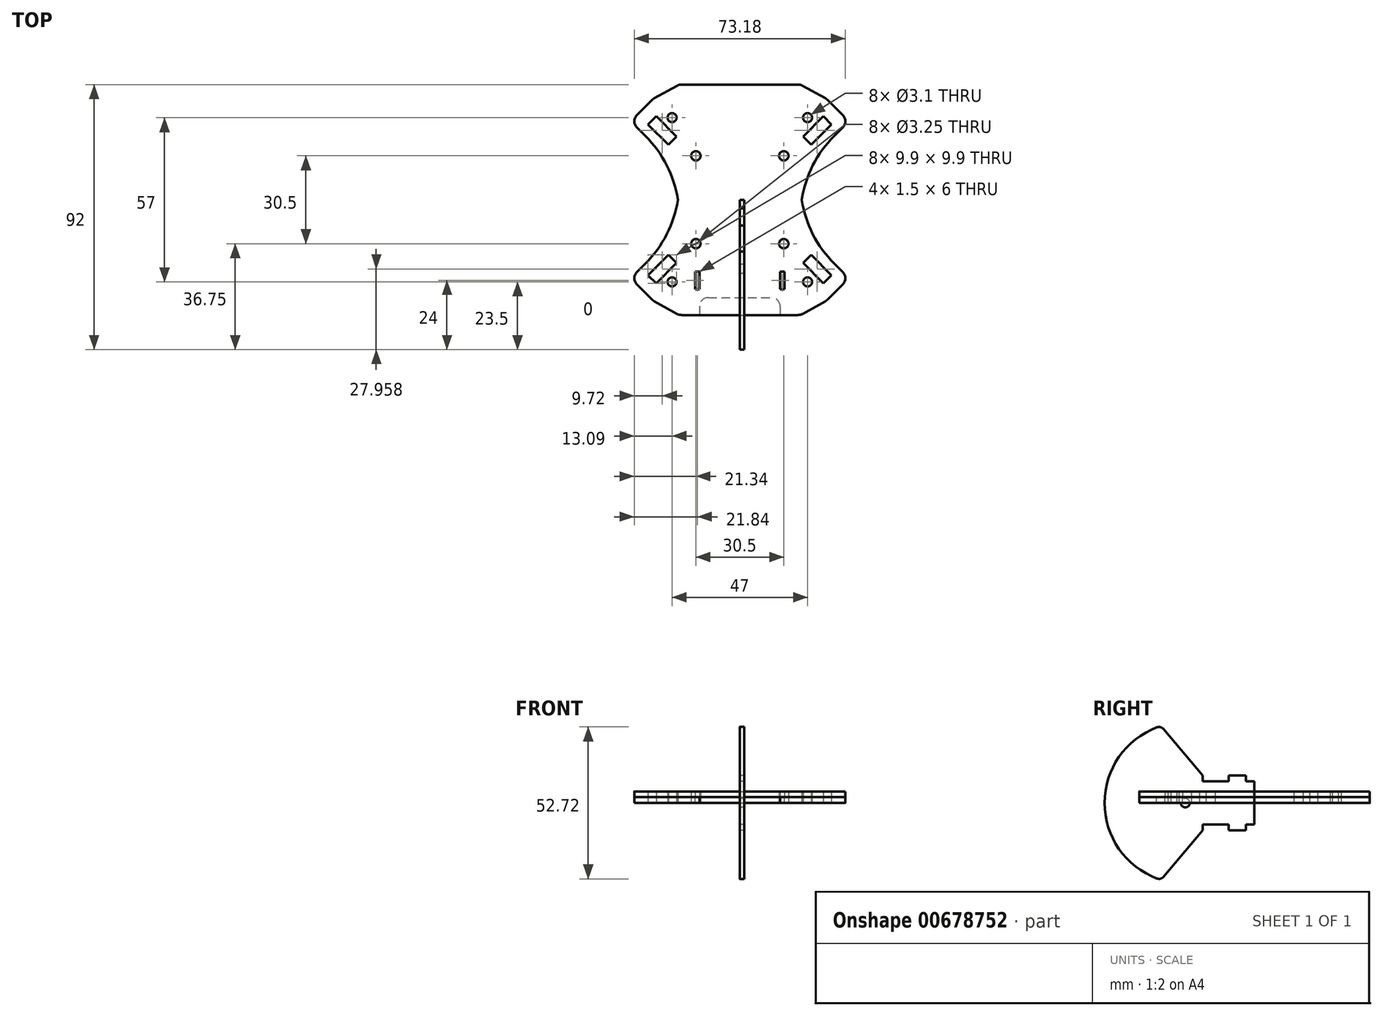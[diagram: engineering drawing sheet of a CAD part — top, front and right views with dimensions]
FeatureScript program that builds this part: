
annotation { "Feature Type Name" : "Feature", "Feature Type Description" : "" }
export const myFeature = defineFeature(function(context is Context, id is Id, definition is map)
    precondition{}
    {
        {
            var Q0;
            Q0=qCreatedBy(makeId("Top.planeOp"),FACE);
            var sketch = newSketch(context, id + "F0", { "sketchPlane" : qUnion([Q0])});
            skLineSegment(sketch, "E0.bottom", {"start": v(-18, 18) * mm, "end": v(18, 18) * mm, "construction": true});
            skLineSegment(sketch, "E0.top", {"start": v(-18, -18) * mm, "end": v(18, -18) * mm, "construction": true});
            skLineSegment(sketch, "E0.left", {"start": v(-18, 18) * mm, "end": v(-18, -18) * mm, "construction": true});
            skLineSegment(sketch, "E0.right", {"start": v(18, 18) * mm, "end": v(18, -18) * mm, "construction": true});
            skPoint(sketch, "E0.middle", {"position": v(0, 0) * mm});
            skLineSegment(sketch, "E1.bottom", {"start": v(-21, 40) * mm, "end": v(0, 40) * mm});
            skCircle(sketch, "E2", {"center": v(-74.25, 74.25) * mm, "radius": 64.25 * mm, "construction": true});
            skCircle(sketch, "E3", {"center": v(-15.25, 15.25) * mm, "radius": 1.63 * mm});
            skLineSegment(sketch, "E4", {"start": v(-15.25, 15.25) * mm, "end": v(0, 0) * mm, "construction": true});
            skLineSegment(sketch, "E5", {"start": v(-74.25, 74.25) * mm, "end": v(0, 0) * mm, "construction": true});
            skLineSegment(sketch, "E6", {"start": v(-32.53, 32.53) * mm, "end": v(-37.83, 27.22) * mm});
            skLineSegment(sketch, "E7", {"start": v(-37.83, 27.22) * mm, "end": v(-32.72, 22.1) * mm});
            skLineSegment(sketch, "E8.trimOffspring", {"start": v(-21, 0) * mm, "end": v(-21, -6.18) * mm});
            skPoint(sketch, "E9.visualSharp", {"position": v(-21, 10.4) * mm});
            skArc(sketch, "E9.filletArc", {"start": v(-21, -6.18) * mm, "mid": v(-24.04, 9.13) * mm, "end": v(-32.72, 22.1) * mm});
            skLineSegment(sketch, "E10", {"start": v(-29, 29) * mm, "end": v(-31.82, 26.16) * mm});
            skLineSegment(sketch, "E11", {"start": v(-31.82, 26.16) * mm, "end": v(-24.75, 19.1) * mm});
            skLineSegment(sketch, "E12", {"start": v(-24.75, 19.1) * mm, "end": v(-21.92, 21.92) * mm});
            skLineSegment(sketch, "E13", {"start": v(-21.92, 21.92) * mm, "end": v(-29, 29) * mm});
            skCircle(sketch, "E14", {"center": v(-23.5, 28.5) * mm, "radius": 1.55 * mm});
            skLineSegment(sketch, "E15", {"start": v(0, 40) * mm, "end": v(0, 0) * mm});
            skLineSegment(sketch, "E16", {"start": v(0, 0) * mm, "end": v(-21, 0) * mm});
            skLineSegment(sketch, "E17", {"start": v(-32.53, 32.53) * mm, "end": v(-30.05, 35) * mm});
            skLineSegment(sketch, "E18", {"start": v(-30.05, 35) * mm, "end": v(-21, 40) * mm});
            skSolve(sketch);
        }
        {
            var Q0;
            Q0=makeQuery(id+"F0.imprint","IMPRINT",FACE,{"disambiguationData":[TD([[makeQuery(id+"F0.imprint","IMPRINT",EDGE,{"derivedFrom":sQuery(id+"F0.wireOp",EDGE,"E1.bottom")}),-1.0]])]});
            extrude(context, id + "F1", {"entities" : qUnion([Q0]), "depth" : 2 * mm, "offsetDistance" : 25 * mm});
        }
        {
            var Q0;
            Q0=makeQuery(id+"F1.opExtrude","SWEPT_BODY",BODY,{"disambiguationData":[OSD([sQuery(id+"F0.wireOp",EDGE,"E1.bottom"),sQuery(id+"F0.wireOp",EDGE,"E3"),sQuery(id+"F0.wireOp",EDGE,"E6"),sQuery(id+"F0.wireOp",EDGE,"E7"),sQuery(id+"F0.wireOp",EDGE,"E8.trimOffspring"),sQuery(id+"F0.wireOp",EDGE,"E9.filletArc"),sQuery(id+"F0.wireOp",EDGE,"E10"),sQuery(id+"F0.wireOp",EDGE,"E11"),sQuery(id+"F0.wireOp",EDGE,"E12"),sQuery(id+"F0.wireOp",EDGE,"E13"),sQuery(id+"F0.wireOp",EDGE,"E14"),sQuery(id+"F0.wireOp",EDGE,"E15"),sQuery(id+"F0.wireOp",EDGE,"E16"),sQuery(id+"F0.wireOp",EDGE,"E17"),sQuery(id+"F0.wireOp",EDGE,"E18")])]});
            var Q1;
            Q1=qCreatedBy(makeId("Right.planeOp"),FACE);
            mirror(context, id + "F2", {"operationType" : NewBodyOperationType.ADD, "entities" : qUnion([Q0]), "mirrorPlane" : qUnion([Q1])});
        }
        {
            var Q0;
            Q0=makeQuery(id+"F1.opExtrude","SWEPT_BODY",BODY,{"disambiguationData":[OSD([sQuery(id+"F0.wireOp",EDGE,"E1.bottom"),sQuery(id+"F0.wireOp",EDGE,"E3"),sQuery(id+"F0.wireOp",EDGE,"E6"),sQuery(id+"F0.wireOp",EDGE,"E7"),sQuery(id+"F0.wireOp",EDGE,"E8.trimOffspring"),sQuery(id+"F0.wireOp",EDGE,"E9.filletArc"),sQuery(id+"F0.wireOp",EDGE,"E10"),sQuery(id+"F0.wireOp",EDGE,"E11"),sQuery(id+"F0.wireOp",EDGE,"E12"),sQuery(id+"F0.wireOp",EDGE,"E13"),sQuery(id+"F0.wireOp",EDGE,"E14"),sQuery(id+"F0.wireOp",EDGE,"E15"),sQuery(id+"F0.wireOp",EDGE,"E16"),sQuery(id+"F0.wireOp",EDGE,"E17"),sQuery(id+"F0.wireOp",EDGE,"E18")])]});
            var Q1;
            Q1=qCreatedBy(makeId("Front.planeOp"),FACE);
            mirror(context, id + "F3", {"operationType" : NewBodyOperationType.ADD, "entities" : qUnion([Q0]), "mirrorPlane" : qUnion([Q1])});
        }
        {
            var Q0;
            Q0=makeQuery(id+"F1.opExtrude","SWEPT_EDGE",EDGE,{"disambiguationData":[OSD([sQuery(id+"F0.wireOp",EDGE,"E6"),sQuery(id+"F0.wireOp",EDGE,"E7")])]});
            var Q1;
            Q1=makeQuery(id+"F1.opExtrude","SWEPT_EDGE",EDGE,{"disambiguationData":[OSD([sQuery(id+"F0.wireOp",EDGE,"E17"),sQuery(id+"F0.wireOp",EDGE,"E18")])]});
            var Q2;
            Q2=makeQuery(id+"F1.opExtrude","SWEPT_EDGE",EDGE,{"disambiguationData":[OSD([sQuery(id+"F0.wireOp",EDGE,"E1.bottom"),sQuery(id+"F0.wireOp",EDGE,"E18")])]});
            var Q3;
            Q3=makeQuery(id+"F2.opPattern","COPY",EDGE,{"derivedFrom":makeQuery(id+"F1.opExtrude","SWEPT_EDGE",EDGE,{"disambiguationData":[OSD([sQuery(id+"F0.wireOp",EDGE,"E1.bottom"),sQuery(id+"F0.wireOp",EDGE,"E18")])]}),"instanceName":"1"});
            var Q4;
            Q4=makeQuery(id+"F2.opPattern","COPY",EDGE,{"derivedFrom":makeQuery(id+"F1.opExtrude","SWEPT_EDGE",EDGE,{"disambiguationData":[OSD([sQuery(id+"F0.wireOp",EDGE,"E17"),sQuery(id+"F0.wireOp",EDGE,"E18")])]}),"instanceName":"1"});
            var Q5;
            Q5=makeQuery(id+"F2.opPattern","COPY",EDGE,{"derivedFrom":makeQuery(id+"F1.opExtrude","SWEPT_EDGE",EDGE,{"disambiguationData":[OSD([sQuery(id+"F0.wireOp",EDGE,"E6"),sQuery(id+"F0.wireOp",EDGE,"E7")])]}),"instanceName":"1"});
            var Q6;
            Q6=makeQuery(id+"F3.opPattern","COPY",EDGE,{"derivedFrom":makeQuery(id+"F2.opPattern","COPY",EDGE,{"derivedFrom":makeQuery(id+"F1.opExtrude","SWEPT_EDGE",EDGE,{"disambiguationData":[OSD([sQuery(id+"F0.wireOp",EDGE,"E6"),sQuery(id+"F0.wireOp",EDGE,"E7")])]}),"instanceName":"1"}),"instanceName":"1"});
            var Q7;
            Q7=makeQuery(id+"F3.opPattern","COPY",EDGE,{"derivedFrom":makeQuery(id+"F2.opPattern","COPY",EDGE,{"derivedFrom":makeQuery(id+"F1.opExtrude","SWEPT_EDGE",EDGE,{"disambiguationData":[OSD([sQuery(id+"F0.wireOp",EDGE,"E17"),sQuery(id+"F0.wireOp",EDGE,"E18")])]}),"instanceName":"1"}),"instanceName":"1"});
            var Q8;
            Q8=makeQuery(id+"F3.opPattern","COPY",EDGE,{"derivedFrom":makeQuery(id+"F2.opPattern","COPY",EDGE,{"derivedFrom":makeQuery(id+"F1.opExtrude","SWEPT_EDGE",EDGE,{"disambiguationData":[OSD([sQuery(id+"F0.wireOp",EDGE,"E1.bottom"),sQuery(id+"F0.wireOp",EDGE,"E18")])]}),"instanceName":"1"}),"instanceName":"1"});
            var Q9;
            Q9=makeQuery(id+"F3.opPattern","COPY",EDGE,{"derivedFrom":makeQuery(id+"F1.opExtrude","SWEPT_EDGE",EDGE,{"disambiguationData":[OSD([sQuery(id+"F0.wireOp",EDGE,"E1.bottom"),sQuery(id+"F0.wireOp",EDGE,"E18")])]}),"instanceName":"1"});
            var Q10;
            Q10=makeQuery(id+"F3.opPattern","COPY",EDGE,{"derivedFrom":makeQuery(id+"F1.opExtrude","SWEPT_EDGE",EDGE,{"disambiguationData":[OSD([sQuery(id+"F0.wireOp",EDGE,"E17"),sQuery(id+"F0.wireOp",EDGE,"E18")])]}),"instanceName":"1"});
            var Q11;
            Q11=makeQuery(id+"F3.opPattern","COPY",EDGE,{"derivedFrom":makeQuery(id+"F1.opExtrude","SWEPT_EDGE",EDGE,{"disambiguationData":[OSD([sQuery(id+"F0.wireOp",EDGE,"E6"),sQuery(id+"F0.wireOp",EDGE,"E7")])]}),"instanceName":"1"});
            fillet(context, id + "F4", {"entities" : qUnion([Q0, Q1, Q2, Q3, Q4, Q5, Q6, Q7, Q8, Q9, Q10, Q11]), "radius" : 3 * mm, "tangentPropagation" : true, "allowEdgeOverflow" : false});
        }
        {
            var Q0;
            {var subQ0=makeQuery(id+"F1.opExtrude","CAP_FACE",FACE,{"disambiguationData":[OSD([sQuery(id+"F0.wireOp",EDGE,"E1.bottom"),sQuery(id+"F0.wireOp",EDGE,"E3"),sQuery(id+"F0.wireOp",EDGE,"E6"),sQuery(id+"F0.wireOp",EDGE,"E7"),sQuery(id+"F0.wireOp",EDGE,"E8.trimOffspring"),sQuery(id+"F0.wireOp",EDGE,"E9.filletArc"),sQuery(id+"F0.wireOp",EDGE,"E10"),sQuery(id+"F0.wireOp",EDGE,"E11"),sQuery(id+"F0.wireOp",EDGE,"E12"),sQuery(id+"F0.wireOp",EDGE,"E13"),sQuery(id+"F0.wireOp",EDGE,"E14"),sQuery(id+"F0.wireOp",EDGE,"E15"),sQuery(id+"F0.wireOp",EDGE,"E16"),sQuery(id+"F0.wireOp",EDGE,"E17"),sQuery(id+"F0.wireOp",EDGE,"E18")])],"isStart":false});var subQ1=makeQuery(id+"F2.boolean.opBoolean","MERGE",FACE,{"derivedFrom":[subQ0,makeQuery(id+"F2.opPattern","COPY",FACE,{"derivedFrom":subQ0,"instanceName":"1"})]});Q0=makeQuery(id+"F3.boolean.opBoolean","MERGE",FACE,{"derivedFrom":[subQ1,makeQuery(id+"F3.opPattern","COPY",FACE,{"derivedFrom":subQ1,"instanceName":"1"})]});}
            var sketch = newSketch(context, id + "F5", { "sketchPlane" : qUnion([Q0])});
            skLineSegment(sketch, "E19.bottom", {"start": v(-15.5, -25) * mm, "end": v(-14, -25) * mm});
            skLineSegment(sketch, "E19.top", {"start": v(-15.5, -31) * mm, "end": v(-14, -31) * mm});
            skLineSegment(sketch, "E19.left", {"start": v(-15.5, -25) * mm, "end": v(-15.5, -31) * mm});
            skLineSegment(sketch, "E19.right", {"start": v(-14, -25) * mm, "end": v(-14, -31) * mm});
            skLineSegment(sketch, "E20.MirrorCS", {"start": v(15.5, -31) * mm, "end": v(14, -31) * mm});
            skLineSegment(sketch, "E21.MirrorCS", {"start": v(15.5, -25) * mm, "end": v(14, -25) * mm});
            skLineSegment(sketch, "E22.MirrorCS", {"start": v(15.5, -25) * mm, "end": v(15.5, -31) * mm});
            skLineSegment(sketch, "E23.MirrorCS", {"start": v(14, -25) * mm, "end": v(14, -31) * mm});
            skSolve(sketch);
        }
        {
            var Q0;
            Q0=makeQuery(id+"F5.imprint","IMPRINT",FACE,{"disambiguationData":[TD([[makeQuery(id+"F5.imprint","IMPRINT",EDGE,{"derivedFrom":sQuery(id+"F5.wireOp",EDGE,"E19.bottom")}),-1.0]])]});
            var Q1;
            Q1=makeQuery(id+"F5.imprint","IMPRINT",FACE,{"disambiguationData":[TD([[makeQuery(id+"F5.imprint","IMPRINT",EDGE,{"derivedFrom":sQuery(id+"F5.wireOp",EDGE,"E20.MirrorCS")}),-1.0]])]});
            extrude(context, id + "F6", {"entities" : qUnion([Q0, Q1]), "operationType" : NewBodyOperationType.REMOVE, "oppositeDirection" : true, "depth" : 25 * mm, "offsetDistance" : 25 * mm});
        }
        {
            var Q0;
            {var subQ0=makeQuery(id+"F1.opExtrude","CAP_FACE",FACE,{"disambiguationData":[OSD([sQuery(id+"F0.wireOp",EDGE,"E1.bottom"),sQuery(id+"F0.wireOp",EDGE,"E3"),sQuery(id+"F0.wireOp",EDGE,"E6"),sQuery(id+"F0.wireOp",EDGE,"E7"),sQuery(id+"F0.wireOp",EDGE,"E8.trimOffspring"),sQuery(id+"F0.wireOp",EDGE,"E9.filletArc"),sQuery(id+"F0.wireOp",EDGE,"E10"),sQuery(id+"F0.wireOp",EDGE,"E11"),sQuery(id+"F0.wireOp",EDGE,"E12"),sQuery(id+"F0.wireOp",EDGE,"E13"),sQuery(id+"F0.wireOp",EDGE,"E14"),sQuery(id+"F0.wireOp",EDGE,"E15"),sQuery(id+"F0.wireOp",EDGE,"E16"),sQuery(id+"F0.wireOp",EDGE,"E17"),sQuery(id+"F0.wireOp",EDGE,"E18")])],"isStart":false});var subQ1=makeQuery(id+"F2.boolean.opBoolean","MERGE",FACE,{"derivedFrom":[subQ0,makeQuery(id+"F2.opPattern","COPY",FACE,{"derivedFrom":subQ0,"instanceName":"1"})]});Q0=makeQuery(id+"F3.boolean.opBoolean","MERGE",FACE,{"derivedFrom":[subQ1,makeQuery(id+"F3.opPattern","COPY",FACE,{"derivedFrom":subQ1,"instanceName":"1"})]});}
            extrude(context, id + "F7", {"entities" : qUnion([Q0]), "depth" : 2 * mm, "offsetDistance" : 25 * mm});
        }
        {
            var Q0;
            {var subQ0=makeQuery(id+"F1.opExtrude","CAP_FACE",FACE,{"disambiguationData":[OSD([sQuery(id+"F0.wireOp",EDGE,"E1.bottom"),sQuery(id+"F0.wireOp",EDGE,"E3"),sQuery(id+"F0.wireOp",EDGE,"E6"),sQuery(id+"F0.wireOp",EDGE,"E7"),sQuery(id+"F0.wireOp",EDGE,"E8.trimOffspring"),sQuery(id+"F0.wireOp",EDGE,"E9.filletArc"),sQuery(id+"F0.wireOp",EDGE,"E10"),sQuery(id+"F0.wireOp",EDGE,"E11"),sQuery(id+"F0.wireOp",EDGE,"E12"),sQuery(id+"F0.wireOp",EDGE,"E13"),sQuery(id+"F0.wireOp",EDGE,"E14"),sQuery(id+"F0.wireOp",EDGE,"E15"),sQuery(id+"F0.wireOp",EDGE,"E16"),sQuery(id+"F0.wireOp",EDGE,"E17"),sQuery(id+"F0.wireOp",EDGE,"E18")])],"isStart":false});var subQ1=makeQuery(id+"F2.boolean.opBoolean","MERGE",FACE,{"derivedFrom":[subQ0,makeQuery(id+"F2.opPattern","COPY",FACE,{"derivedFrom":subQ0,"instanceName":"1"})]});Q0=makeQuery(id+"F3.boolean.opBoolean","MERGE",FACE,{"derivedFrom":[subQ1,makeQuery(id+"F3.opPattern","COPY",FACE,{"derivedFrom":subQ1,"instanceName":"1"})]});}
            var sketch = newSketch(context, id + "F8", { "sketchPlane" : qUnion([Q0])});
            skLineSegment(sketch, "E24.bottom", {"start": v(-11, -34) * mm, "end": v(11, -34) * mm});
            skLineSegment(sketch, "E24.top", {"start": v(-14, -40) * mm, "end": v(14, -40) * mm});
            skLineSegment(sketch, "E24.left", {"start": v(-14, -37) * mm, "end": v(-14, -40) * mm});
            skLineSegment(sketch, "E24.right", {"start": v(14, -37) * mm, "end": v(14, -40) * mm});
            skPoint(sketch, "E25.visualSharp", {"position": v(-14, -34) * mm});
            skArc(sketch, "E25.filletArc", {"start": v(-11, -34) * mm, "mid": v(-13.12, -34.88) * mm, "end": v(-14, -37) * mm});
            skPoint(sketch, "E26.visualSharp", {"position": v(14, -34) * mm});
            skArc(sketch, "E26.filletArc", {"start": v(14, -37) * mm, "mid": v(13.12, -34.88) * mm, "end": v(11, -34) * mm});
            skSolve(sketch);
        }
        {
            var Q0;
            Q0 = qSketchRegion(id + "F8", true);
            extrude(context, id + "F9", {"entities" : qUnion([Q0]), "operationType" : NewBodyOperationType.REMOVE, "oppositeDirection" : true, "depth" : 25 * mm, "offsetDistance" : 25 * mm});
        }
        {
            var Q0;
            Q0 = qSketchRegion(id + "F8", true);
            extrude(context, id + "F10", {"entities" : qUnion([Q0]), "operationType" : NewBodyOperationType.REMOVE, "oppositeDirection" : true, "depth" : 25 * mm, "offsetDistance" : 25 * mm});
        }
        {
            var Q0;
            Q0=qCreatedBy(makeId("Right.planeOp"),FACE);
            var sketch = newSketch(context, id + "F11", { "sketchPlane" : qUnion([Q0])});
            skLineSegment(sketch, "E27", {"start": v(0, 7.5) * mm, "end": v(-3, 7.5) * mm});
            skLineSegment(sketch, "E28", {"start": v(-3, 7.5) * mm, "end": v(-3, 9.5) * mm});
            skLineSegment(sketch, "E29", {"start": v(-3, 9.5) * mm, "end": v(-9, 9.5) * mm});
            skLineSegment(sketch, "E30", {"start": v(-9, 9.5) * mm, "end": v(-9, 7.5) * mm});
            skLineSegment(sketch, "E31", {"start": v(-9, 7.5) * mm, "end": v(-18, 7.5) * mm});
            skLineSegment(sketch, "E32", {"start": v(-18, 7.5) * mm, "end": v(-18, 9.5) * mm});
            skLineSegment(sketch, "E33", {"start": v(-18, 9.5) * mm, "end": v(-31.55, 25.65) * mm});
            skCircle(sketch, "E34", {"center": v(-24, 0) * mm, "radius": 1.55 * mm});
            skArc(sketch, "E35", {"start": v(-33.78, 26.24) * mm, "mid": v(-47, 15.97) * mm, "end": v(-52, 0) * mm});
            skPoint(sketch, "E36.visualSharp", {"position": v(-32.43, 26.7) * mm});
            skArc(sketch, "E36.filletArc", {"start": v(-31.55, 25.65) * mm, "mid": v(-32.57, 26.3) * mm, "end": v(-33.78, 26.24) * mm});
            skLineSegment(sketch, "E37", {"start": v(0, 7.5) * mm, "end": v(0, 0) * mm});
            skLineSegment(sketch, "E38.MirrorCS", {"start": v(-9, -9.5) * mm, "end": v(-9, -7.5) * mm});
            skLineSegment(sketch, "E39.MirrorCS", {"start": v(-3, -7.5) * mm, "end": v(-3, -9.5) * mm});
            skLineSegment(sketch, "E40.MirrorCS", {"start": v(-18, -7.5) * mm, "end": v(-18, -9.5) * mm});
            skArc(sketch, "E41.MirrorCS", {"start": v(-31.55, -25.65) * mm, "mid": v(-32.57, -26.3) * mm, "end": v(-33.78, -26.24) * mm});
            skLineSegment(sketch, "E42.MirrorCS", {"start": v(-9, -7.5) * mm, "end": v(-18, -7.5) * mm});
            skLineSegment(sketch, "E43.MirrorCS", {"start": v(-3, -9.5) * mm, "end": v(-9, -9.5) * mm});
            skLineSegment(sketch, "E44.MirrorCS", {"start": v(-18, -9.5) * mm, "end": v(-31.55, -25.65) * mm});
            skPoint(sketch, "E45.MirrorP", {"position": v(-32.43, -26.7) * mm});
            skLineSegment(sketch, "E46.MirrorCS", {"start": v(0, -7.5) * mm, "end": v(-3, -7.5) * mm});
            skLineSegment(sketch, "E47.MirrorCS", {"start": v(0, -7.5) * mm, "end": v(0, 0) * mm});
            skArc(sketch, "E48.MirrorCS", {"start": v(-33.78, -26.24) * mm, "mid": v(-47, -15.97) * mm, "end": v(-52, 0) * mm});
            skSolve(sketch);
        }
        {
            var Q0;
            Q0=makeQuery(id+"F11.imprint","IMPRINT",FACE,{"disambiguationData":[TD([[makeQuery(id+"F11.imprint","IMPRINT",EDGE,{"derivedFrom":sQuery(id+"F11.wireOp",EDGE,"E27")}),1.0]])]});
            extrude(context, id + "F12", {"entities" : qUnion([Q0]), "depth" : 1.5 * mm, "offsetDistance" : 25 * mm});
        }
    });
